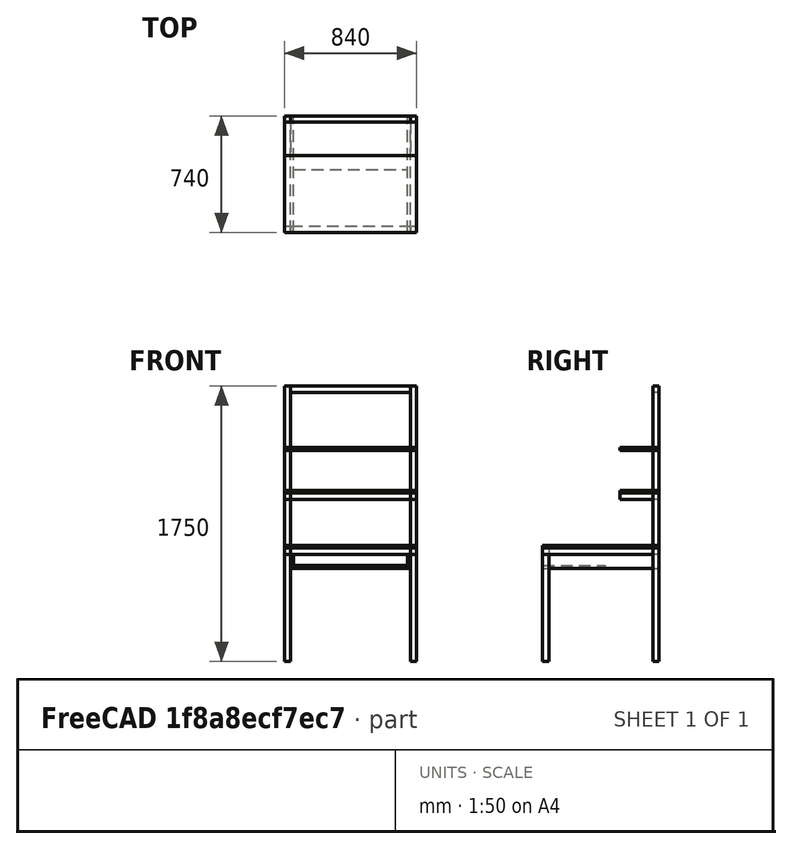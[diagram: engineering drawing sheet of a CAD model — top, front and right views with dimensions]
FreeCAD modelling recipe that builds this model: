
FCSTD DOCUMENT  (FreeCAD 0.19R24267 +99 (Git))
Label: 工具桌
License: All rights reserved
LicenseURL: http://en.wikipedia.org/wiki/All_rights_reserved
objects: Part::Box×22, App::Part×3
note: 22 computed .brp shape members not serialized (recipe doc carries the construction recipe); baked Part::Feature solids carry a one-line shape summary decoded from their .brp

FEATURE [Part::Box] Box  label="立方体"
  AttacherType = Attacher::AttachEngine3D
  Height = 680
  Length = 40
  Width = 40
FEATURE [Part::Box] Box001  label="立方体001"
  AttacherType = Attacher::AttachEngine3D
  Height = 680
  Length = 40
  Placement = pos=(800,0,0) rot=(0,0,1;0rad)
  Width = 40
FEATURE [Part::Box] Box002  label="立方体002"
  AttacherType = Attacher::AttachEngine3D
  Height = 1750
  Length = 40
  Placement = pos=(0,700,0) rot=(0,0,1;0rad)
  Width = 40
FEATURE [Part::Box] Box003  label="立方体003"
  AttacherType = Attacher::AttachEngine3D
  Height = 1750
  Length = 40
  Placement = pos=(800,700,0) rot=(0,0,1;0rad)
  Width = 40
FEATURE [Part::Box] Box004  label="立方体004"
  AttacherType = Attacher::AttachEngine3D
  Height = 700
  Length = 40
  Placement = pos=(800,1.599e-13,720) rot=(1,0,0;4.71239rad)
  Width = 40
FEATURE [Part::Box] Box005  label="立方体005"
  AttacherType = Attacher::AttachEngine3D
  Height = 700
  Length = 40
  Placement = pos=(800,1.6e-13,720) rot=(-1,0,0;1.5708rad)
  Width = 40
FEATURE [Part::Box] Box006  label="立方体006"
  AttacherType = Attacher::AttachEngine3D
  Height = 700
  Length = 40
  Placement = pos=(0,1.6e-13,720) rot=(-1,0,0;1.5708rad)
  Width = 40
FEATURE [Part::Box] Box007  label="立方体007"
  AttacherType = Attacher::AttachEngine3D
  Height = 760
  Length = 40
  Placement = pos=(40,40,720) rot=(-0.57735,0.57735,-0.57735;2.0944rad)
  Width = 40
FEATURE [Part::Box] Box008  label="立方体008"
  AttacherType = Attacher::AttachEngine3D
  Height = 760
  Length = 40
  Placement = pos=(40,40,720) rot=(0.57735,-0.57735,0.57735;4.18879rad)
  Width = 40
FEATURE [Part::Box] Box009  label="立方体009"
  AttacherType = Attacher::AttachEngine3D
  Height = 760
  Length = 40
  Placement = pos=(40,740,720) rot=(0.57735,-0.57735,0.57735;4.18879rad)
  Width = 40
FEATURE [Part::Box] Box010  label="立方体010"
  AttacherType = Attacher::AttachEngine3D
  Height = 760
  Length = 40
  Placement = pos=(40,740,1750) rot=(0.57735,-0.57735,0.57735;4.18879rad)
  Width = 40
FEATURE [Part::Box] Box011  label="立方体011"
  AttacherType = Attacher::AttachEngine3D
  Height = 210
  Length = 40
  Placement = pos=(840,700,1070) rot=(0,0.707107,-0.707107;3.14159rad)
  Width = 40
FEATURE [Part::Box] Box012  label="立方体012"
  AttacherType = Attacher::AttachEngine3D
  Height = 210
  Length = 40
  Placement = pos=(40,700,1070) rot=(0,0.707107,-0.707107;3.14159rad)
  Width = 40
FEATURE [Part::Box] Box017  label="立方体017"
  AttacherType = Attacher::AttachEngine3D
  Height = 210
  Length = 40
  Placement = pos=(40,700,1070) rot=(0,0.707107,-0.707107;3.14159rad)
  Width = 40
FEATURE [Part::Box] Box018  label="立方体018"
  AttacherType = Attacher::AttachEngine3D
  Height = 210
  Length = 40
  Placement = pos=(840,700,1070) rot=(0,0.707107,-0.707107;3.14159rad)
  Width = 40
FEATURE [App::Part] Part
  Group = -> [Box017,Box018]
  Origin = -> Origin
  Placement = pos=(0,0,270) rot=(0,0,1;0rad)
FEATURE [Part::Box] Box013  label="立方体013"
  AttacherType = Attacher::AttachEngine3D
  Height = 760
  Length = 40
  Placement = pos=(40,740,1070) rot=(0.57735,-0.57735,0.57735;4.18879rad)
  Width = 40
FEATURE [App::Part] Part001  label="抽屉"
  Origin = -> Origin001
FEATURE [Part::Box] Box019  label="立方体019"
  AttacherType = Attacher::AttachEngine3D
  Height = 724
  Length = 400
  Placement = pos=(58,1.634e-13,592) rot=(-0.57735,-0.57735,-0.57735;4.18879rad)
  Width = 18
FEATURE [Part::Box] Box020  label="立方体020"
  AttacherType = Attacher::AttachEngine3D
  Height = 18
  Length = 740
  Placement = pos=(40,1.63e-13,592) rot=(0.57735,0.57735,0.57735;2.0944rad)
  Width = 88
FEATURE [Part::Box] Box021  label="立方体021"
  AttacherType = Attacher::AttachEngine3D
  Height = 18
  Length = 740
  Placement = pos=(782,1.63e-13,592) rot=(0.57735,0.57735,0.57735;2.0944rad)
  Width = 88
FEATURE [Part::Box] Box022  label="立方体022"
  AttacherType = Attacher::AttachEngine3D
  Height = 840
  Length = 250
  Placement = pos=(2.84e-14,490,1070) rot=(0.57735,0.57735,0.57735;2.0944rad)
  Width = 18
FEATURE [Part::Box] Box023  label="立方体023"
  AttacherType = Attacher::AttachEngine3D
  Height = 840
  Length = 250
  Placement = pos=(2.8e-14,490,1340) rot=(0.57735,0.57735,0.57735;2.0944rad)
  Width = 18
FEATURE [Part::Box] Box024  label="立方体024"
  AttacherType = Attacher::AttachEngine3D
  Height = 840
  Length = 740
  Placement = pos=(2.8e-14,1.705e-13,720) rot=(0.57735,0.57735,0.57735;2.0944rad)
  Width = 18
FEATURE [App::Part] Part002
  Group = -> [Box022,Box023,Box024]
  Origin = -> Origin002
